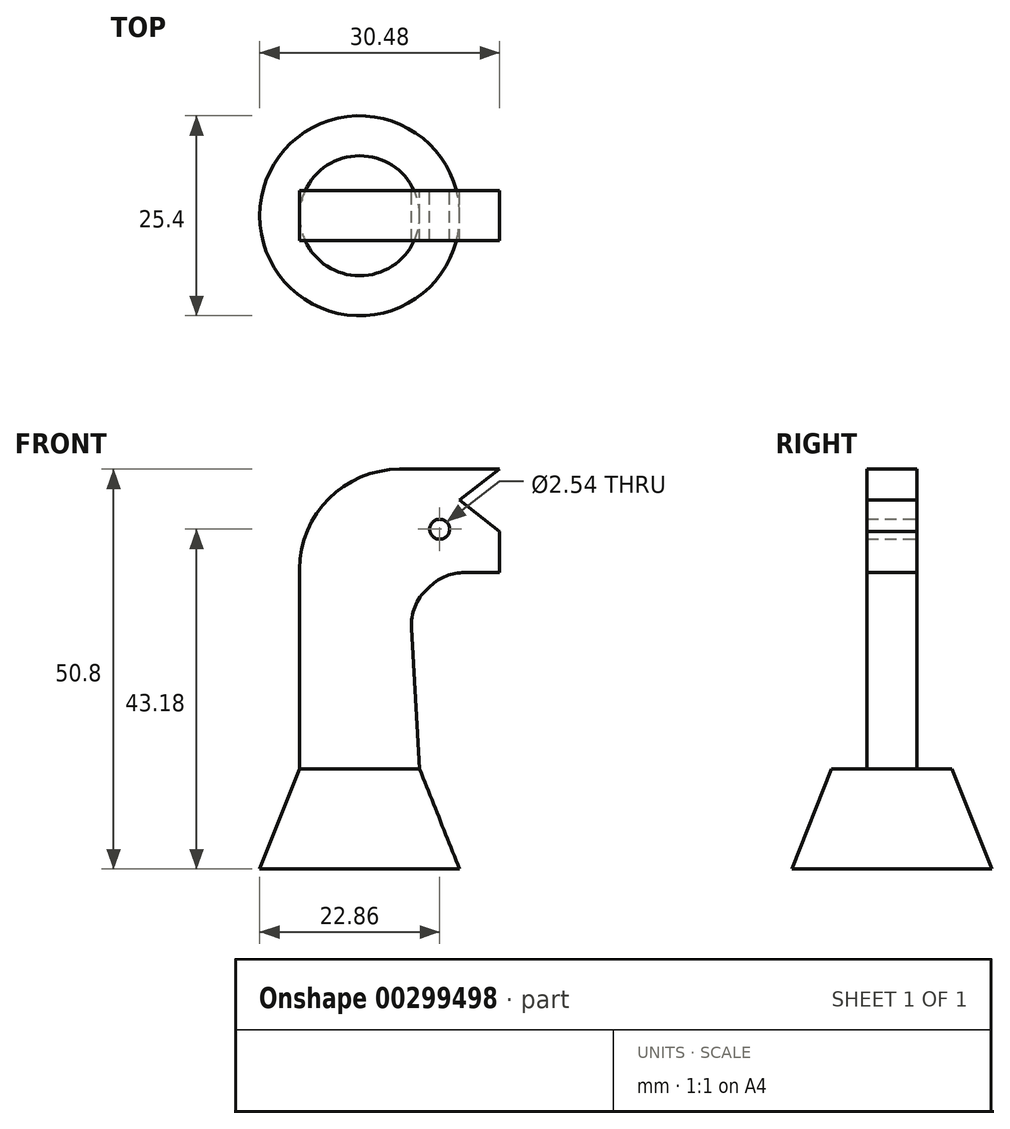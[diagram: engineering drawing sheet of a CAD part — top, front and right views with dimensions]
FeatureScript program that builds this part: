
annotation { "Feature Type Name" : "Feature", "Feature Type Description" : "" }
export const myFeature = defineFeature(function(context is Context, id is Id, definition is map)
    precondition{}
    {
        {
            var Q0;
            Q0=qCreatedBy(makeId("Front.planeOp"),FACE);
            var sketch = newSketch(context, id + "F0", { "sketchPlane" : qUnion([Q0])});
            skLineSegment(sketch, "E0", {"start": v(0, 0) * mm, "end": v(25.4, 0) * mm});
            skLineSegment(sketch, "E1", {"start": v(25.4, 0) * mm, "end": v(20.32, 12.7) * mm});
            skLineSegment(sketch, "E2", {"start": v(20.32, 12.7) * mm, "end": v(5.08, 12.7) * mm});
            skLineSegment(sketch, "E3", {"start": v(5.08, 12.7) * mm, "end": v(0, 0) * mm});
            skLineSegment(sketch, "E4", {"start": v(12.7, 12.7) * mm, "end": v(12.7, 0) * mm});
            skSolve(sketch);
        }
        {
            var Q0;
            {var subQ0=sQuery(id+"F0.wireOp",EDGE,"E1");Q0=makeQuery(id+"F0.imprint","IMPRINT",FACE,{"disambiguationData":[TD([[makeQuery(id+"F0.imprint","IMPRINT",EDGE,{"derivedFrom":subQ0}),1.0]])]});}
            var Q1;
            Q1=sQuery(id+"F0.wireOp",EDGE,"E4");
            revolve(context, id + "F1", {"entities" : qUnion([Q0]), "axis" : qUnion([Q1]), "revolveType" : RevolveType.FULL});
        }
        {
            var Q0;
            Q0=qCreatedBy(makeId("Front.planeOp"),FACE);
            var sketch = newSketch(context, id + "F2", { "sketchPlane" : qUnion([Q0])});
            skLineSegment(sketch, "E5", {"start": v(5.08, 12.7) * mm, "end": v(5.08, 38.1) * mm});
            skLineSegment(sketch, "E6", {"start": v(17.78, 50.8) * mm, "end": v(30.48, 50.8) * mm});
            skLineSegment(sketch, "E7", {"start": v(30.48, 50.8) * mm, "end": v(25.4, 46.86) * mm});
            skLineSegment(sketch, "E8", {"start": v(25.4, 46.86) * mm, "end": v(30.48, 42.92) * mm});
            skLineSegment(sketch, "E9", {"start": v(30.48, 50.8) * mm, "end": v(30.48, 42.92) * mm, "construction": true});
            skLineSegment(sketch, "E10", {"start": v(30.48, 42.92) * mm, "end": v(30.48, 37.67) * mm});
            skLineSegment(sketch, "E11", {"start": v(30.48, 37.67) * mm, "end": v(26.02, 37.67) * mm});
            skLineSegment(sketch, "E12", {"start": v(21.3, 35.6) * mm, "end": v(21.7, 35.98) * mm});
            skLineSegment(sketch, "E13", {"start": v(19.27, 30.58) * mm, "end": v(20.32, 12.7) * mm});
            skLineSegment(sketch, "E14", {"start": v(20.32, 12.7) * mm, "end": v(5.08, 12.7) * mm});
            skCircle(sketch, "E15", {"center": v(22.86, 43.18) * mm, "radius": 1.27 * mm});
            skLineSegment(sketch, "E16", {"start": v(30.48, 46.86) * mm, "end": v(25.4, 46.86) * mm, "construction": true});
            skPoint(sketch, "E17.visualSharp", {"position": v(5.08, 50.8) * mm});
            skArc(sketch, "E17.filletArc", {"start": v(17.78, 50.8) * mm, "mid": v(8.8, 47.08) * mm, "end": v(5.08, 38.1) * mm});
            skPoint(sketch, "E18.visualSharp", {"position": v(23.53, 37.67) * mm});
            skArc(sketch, "E18.filletArc", {"start": v(26.02, 37.67) * mm, "mid": v(23.7, 37.23) * mm, "end": v(21.7, 35.98) * mm});
            skPoint(sketch, "E19.visualSharp", {"position": v(19.1, 33.57) * mm});
            skArc(sketch, "E19.filletArc", {"start": v(21.3, 35.6) * mm, "mid": v(19.72, 33.32) * mm, "end": v(19.27, 30.58) * mm});
            skSolve(sketch);
        }
        {
            var Q0;
            Q0=makeQuery(id+"F2.imprint","IMPRINT",FACE,{"disambiguationData":[TD([[makeQuery(id+"F2.imprint","IMPRINT",EDGE,{"derivedFrom":sQuery(id+"F2.wireOp",EDGE,"E5")}),-1.0]])]});
            extrude(context, id + "F3", {"entities" : qUnion([Q0]), "operationType" : NewBodyOperationType.ADD, "endBound" : BoundingType.SYMMETRIC, "depth" : 6.35 * mm});
        }
    });
